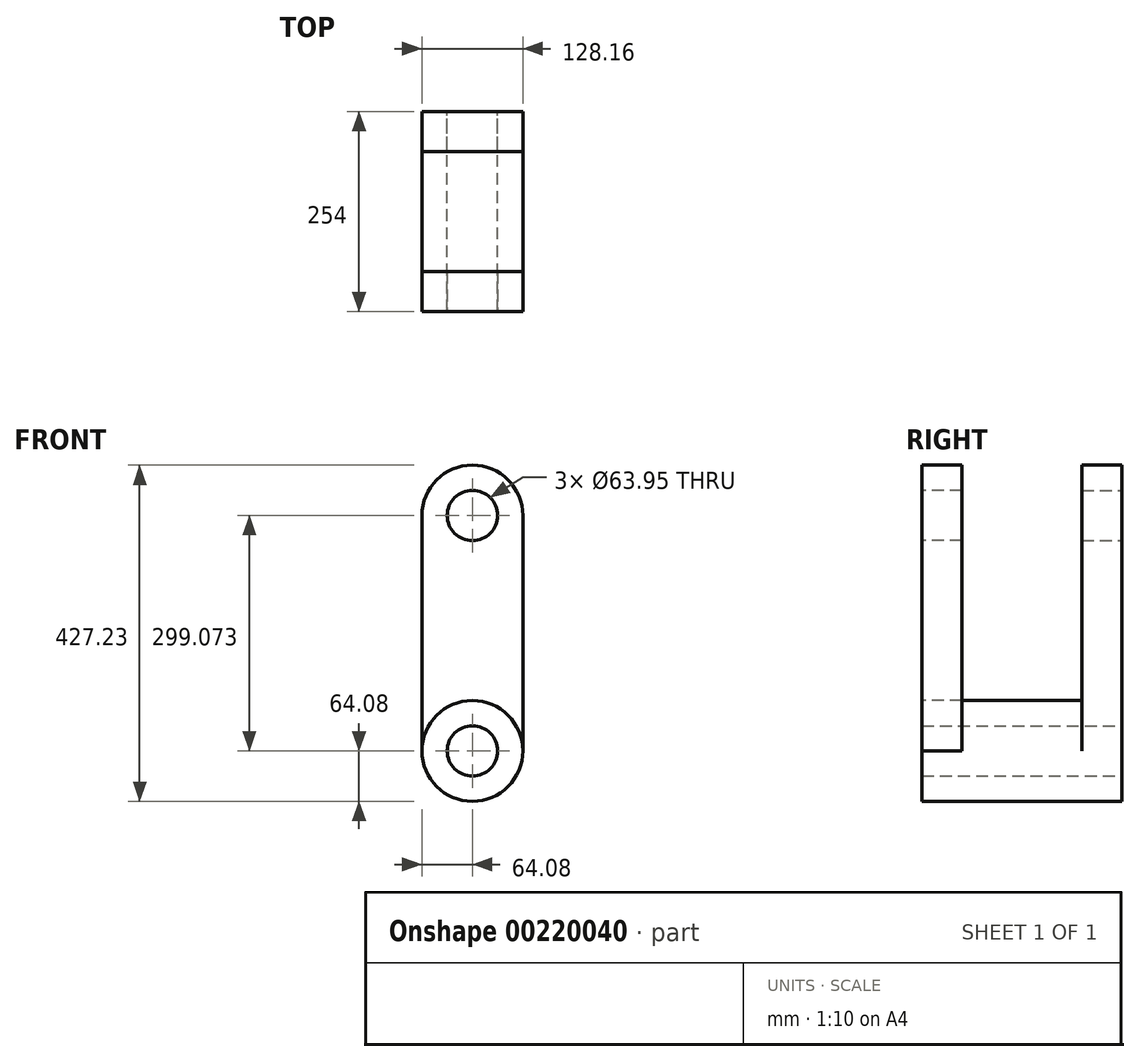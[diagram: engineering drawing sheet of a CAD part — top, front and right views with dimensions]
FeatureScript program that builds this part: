
annotation { "Feature Type Name" : "Feature", "Feature Type Description" : "" }
export const myFeature = defineFeature(function(context is Context, id is Id, definition is map)
    precondition{}
    {
        {
            var Q0;
            Q0=qCreatedBy(makeId("Front.planeOp"),FACE);
            var sketch = newSketch(context, id + "F0", { "sketchPlane" : qUnion([Q0])});
            skCircle(sketch, "E0", {"center": v(0, 0) * mm, "radius": 64.08 * mm});
            skCircle(sketch, "E1", {"center": v(0, 0) * mm, "radius": 31.97 * mm});
            skSolve(sketch);
        }
        {
            var Q0;
            Q0=makeQuery(id+"F0.imprint","IMPRINT",FACE,{"disambiguationData":[TD([[makeQuery(id+"F0.imprint","IMPRINT",EDGE,{"derivedFrom":sQuery(id+"F0.wireOp",EDGE,"E0")}),1.0]])]});
            extrude(context, id + "F1", {"entities" : qUnion([Q0]), "depth" : 254 * mm});
        }
        {
            var Q0;
            Q0=makeQuery(id+"F1.opExtrude","CAP_FACE",FACE,{"disambiguationData":[OSD([sQuery(id+"F0.wireOp",EDGE,"E0"),sQuery(id+"F0.wireOp",EDGE,"E1")])],"isStart":true});
            var sketch = newSketch(context, id + "F2", { "sketchPlane" : qUnion([Q0])});
            skCircle(sketch, "E2.0.0", {"center": v(0, 0) * mm, "radius": 64.08 * mm});
            skLineSegment(sketch, "E3.left", {"start": v(64.08, 0) * mm, "end": v(64.08, 0) * mm});
            skLineSegment(sketch, "E3.right", {"start": v(-64.08, 0) * mm, "end": v(-64.08, 0) * mm});
            skLineSegment(sketch, "E4.left", {"start": v(-64.08, 0) * mm, "end": v(-64.08, 299.07) * mm});
            skLineSegment(sketch, "E4.right", {"start": v(64.08, 0) * mm, "end": v(64.08, 299.07) * mm});
            skArc(sketch, "E5.MirrorC", {"start": v(-64.08, 299.07) * mm, "mid": v(0, 363.15) * mm, "end": v(64.08, 299.07) * mm});
            skCircle(sketch, "E6.0", {"center": v(0, 0) * mm, "radius": 31.97 * mm});
            skCircle(sketch, "E7.MirrorC", {"center": v(0, 299.07) * mm, "radius": 31.97 * mm});
            skPoint(sketch, "E8.end.orphan", {"position": v(-64.08, 149.54) * mm});
            skPoint(sketch, "E8.start.orphan", {"position": v(64.08, 149.54) * mm});
            skSolve(sketch);
        }
        {
            var Q0;
            Q0 = qSketchRegion(id + "F2", true);
            extrude(context, id + "F3", {"entities" : qUnion([Q0]), "operationType" : NewBodyOperationType.ADD, "oppositeDirection" : true, "depth" : 50.8 * mm});
        }
        {
            var Q0;
            Q0=makeQuery(id+"F1.opExtrude","CAP_FACE",FACE,{"disambiguationData":[OSD([sQuery(id+"F0.wireOp",EDGE,"E0"),sQuery(id+"F0.wireOp",EDGE,"E1")])],"isStart":false});
            var sketch = newSketch(context, id + "F4", { "sketchPlane" : qUnion([Q0])});
            skCircle(sketch, "E9.0", {"center": v(0, 299.07) * mm, "radius": 31.97 * mm});
            skArc(sketch, "E10.0", {"start": v(64.08, 299.07) * mm, "mid": v(0, 363.15) * mm, "end": v(-64.08, 299.07) * mm});
            skLineSegment(sketch, "E11.0", {"start": v(64.08, 0) * mm, "end": v(64.08, 299.07) * mm});
            skLineSegment(sketch, "E12.0", {"start": v(-64.08, 0) * mm, "end": v(-64.08, 299.07) * mm});
            skCircle(sketch, "E13.0", {"center": v(0, 0) * mm, "radius": 64.08 * mm});
            skCircle(sketch, "E14.0", {"center": v(0, 0) * mm, "radius": 31.97 * mm});
            skSolve(sketch);
        }
        {
            var Q0;
            Q0=makeQuery(id+"F4.imprint","IMPRINT",FACE,{"disambiguationData":[TD([[makeQuery(id+"F4.imprint","IMPRINT",EDGE,{"derivedFrom":sQuery(id+"F4.wireOp",EDGE,"E9.0")}),-1.0]])]});
            extrude(context, id + "F5", {"entities" : qUnion([Q0]), "oppositeDirection" : true, "depth" : 50.8 * mm});
        }
    });
